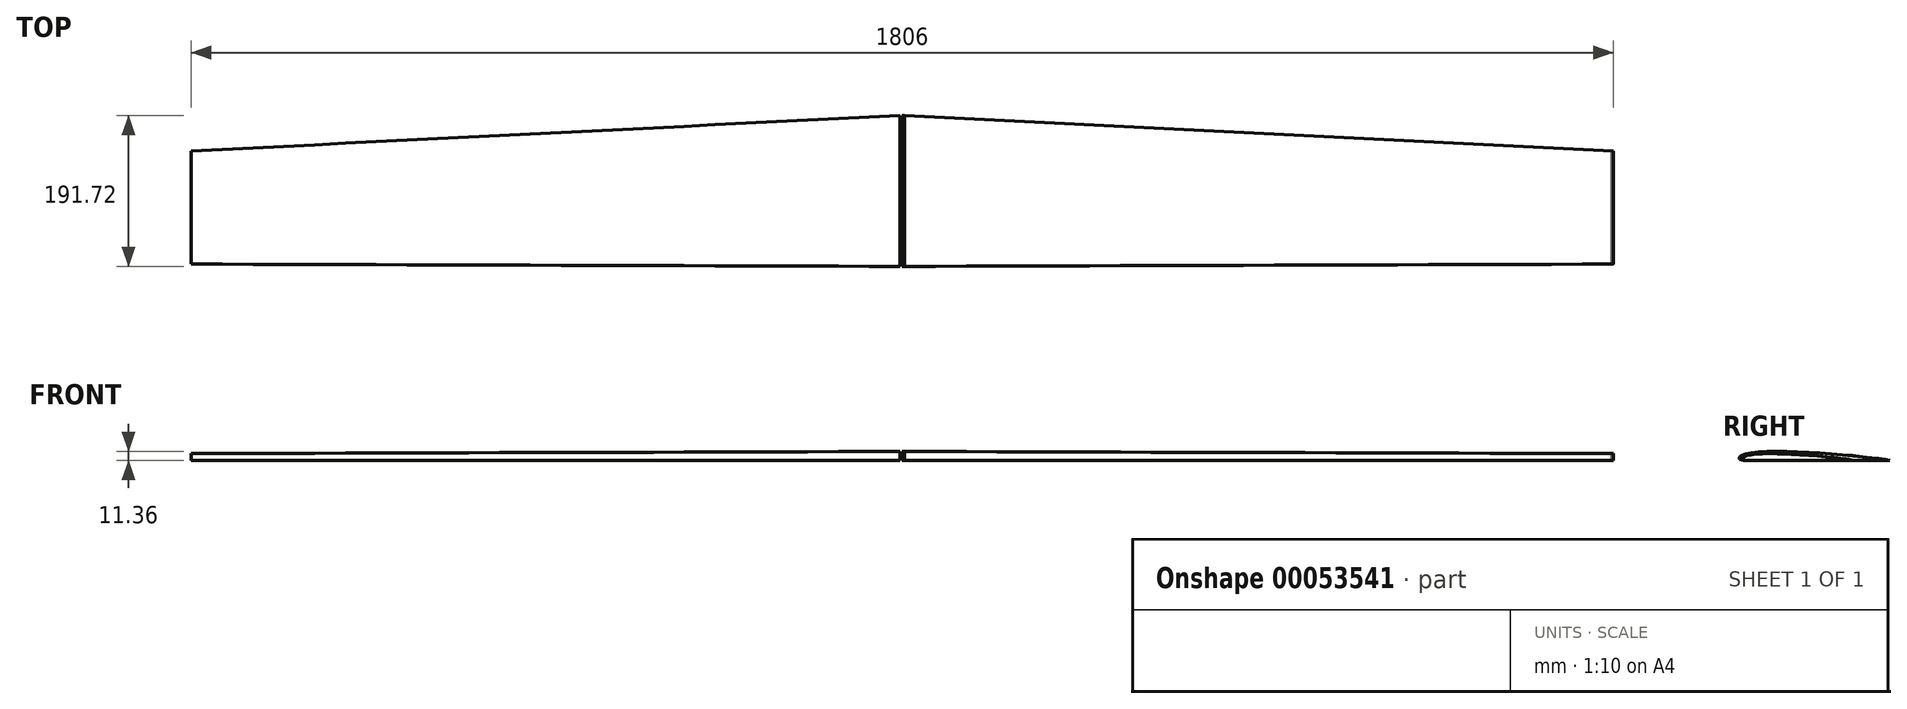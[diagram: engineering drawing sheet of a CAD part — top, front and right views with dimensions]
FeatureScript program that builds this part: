
annotation { "Feature Type Name" : "Feature", "Feature Type Description" : "" }
export const myFeature = defineFeature(function(context is Context, id is Id, definition is map)
    precondition{}
    {
        {
            var Q0;
            Q0=qCreatedBy(makeId("Right.planeOp"),FACE);
            var sketch = newSketch(context, id + "F0", { "sketchPlane" : qUnion([Q0])});
            skLineSegment(sketch, "E0", {"start": v(0, 0) * mm, "end": v(180, 0) * mm});
            skFitSpline(sketch, "E1", {"points": [v(0, 0) * mm, v(-10.97, 1.13) * mm, v(-0.78, 8.46) * mm, v(180, 0) * mm], "startDerivative": vector(-26.9, 0) * mm, "endDerivative": vector(115.45, -21.9) * mm});
            skLineSegment(sketch, "E2.filletArc", {"start": v(0, 0) * mm, "end": v(0, 0) * mm});
            skPoint(sketch, "E3", {"position": v(-4.48, 0) * mm});
            skPoint(sketch, "E4", {"position": v(-2.25, 8.1) * mm});
            skPoint(sketch, "E5", {"position": v(4.32, 9.44) * mm});
            skSolve(sketch);
        }
        {
            var Q0;
            Q0 = qSketchRegion(id + "F0", true);
            extrude(context, id + "F1", {"entities" : qUnion([Q0]), "depth" : 3 * mm});
        }
        {
            var Q0;
            Q0=makeQuery(id+"F1.opExtrude","SWEPT_BODY",BODY,{"disambiguationData":[OSD([sQuery(id+"F0.wireOp",EDGE,"E0"),sQuery(id+"F0.wireOp",EDGE,"E1"),sQuery(id+"F0.wireOp",EDGE,"E2.filletArc")])]});
            var Q1;
            Q1=qCreatedBy(makeId("Right.planeOp"),FACE);
            transform(context, id + "F2", {"entities" : qUnion([Q0]), "transformType" : TransformType.TRANSLATION_DISTANCE, "transformDirection" : qUnion([Q1]), "distance" : 900 * mm, "makeCopy" : true});
        }
        {
            var Q0;
            Q0=makeQuery(id+"F2.opPattern","COPY",BODY,{"derivedFrom":makeQuery(id+"F1.opExtrude","SWEPT_BODY",BODY,{"disambiguationData":[OSD([sQuery(id+"F0.wireOp",EDGE,"E0"),sQuery(id+"F0.wireOp",EDGE,"E1"),sQuery(id+"F0.wireOp",EDGE,"E2.filletArc")])]}),"instanceName":"1"});
            var Q1;
            Q1=makeQuery(id+"F2.opPattern","COPY",VERTEX,{"derivedFrom":makeQuery(id+"F1.opExtrude","CAP_VERTEX",VERTEX,{"disambiguationData":[OSD([sQuery(id+"F0.wireOp",EDGE,"E1"),sQuery(id+"F0.wireOp",EDGE,"E2.filletArc")])],"isStart":false}),"instanceName":"1"});
            transform(context, id + "F3", {"entities" : qUnion([Q0]), "transformType" : TransformType.SCALE_UNIFORMLY, "scale" : .75, "scalePoint" : qUnion([Q1]), "makeCopy" : false});
        }
        {
            var Q0;
            Q0=makeQuery(id+"F1.opExtrude","CAP_FACE",FACE,{"disambiguationData":[OSD([sQuery(id+"F0.wireOp",EDGE,"E0"),sQuery(id+"F0.wireOp",EDGE,"E1"),sQuery(id+"F0.wireOp",EDGE,"E2.filletArc")])],"isStart":false});
            var Q1;
            Q1=makeQuery(id+"F2.opPattern","COPY",FACE,{"derivedFrom":makeQuery(id+"F1.opExtrude","CAP_FACE",FACE,{"disambiguationData":[OSD([sQuery(id+"F0.wireOp",EDGE,"E0"),sQuery(id+"F0.wireOp",EDGE,"E1"),sQuery(id+"F0.wireOp",EDGE,"E2.filletArc")])],"isStart":false}),"instanceName":"1"});
            loft(context, id + "F4", {"sheetProfilesArray" : [{ "sheetProfileEntities" : qUnion([Q0]) }, { "sheetProfileEntities" : qUnion([Q1]) }]});
        }
        {
            var Q0;
            Q0=makeQuery(id+"F4.opLoft","SWEPT_BODY",BODY,{"disambiguationData":[OSD([sQuery(id+"F0.wireOp",EDGE,"E0"),sQuery(id+"F0.wireOp",EDGE,"E1")])]});
            var Q1;
            Q1=qCreatedBy(makeId("Right.planeOp"),FACE);
            mirror(context, id + "F5", {"entities" : qUnion([Q0]), "mirrorPlane" : qUnion([Q1])});
        }
    });
